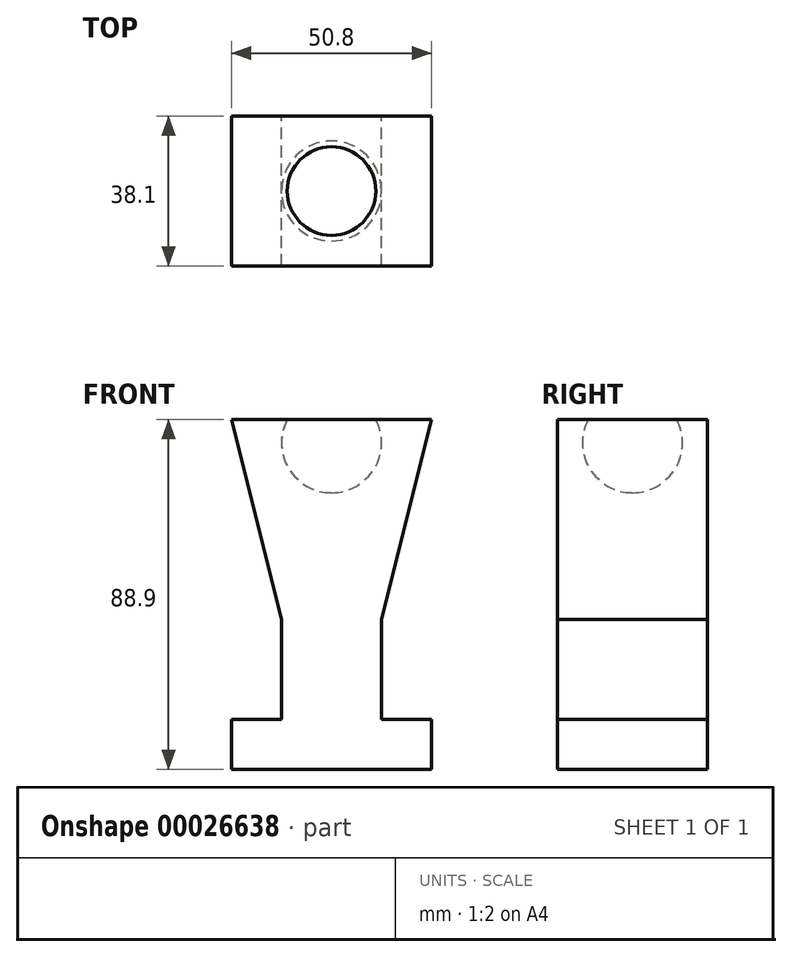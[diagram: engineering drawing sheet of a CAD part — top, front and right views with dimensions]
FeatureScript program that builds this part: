
annotation { "Feature Type Name" : "Feature", "Feature Type Description" : "" }
export const myFeature = defineFeature(function(context is Context, id is Id, definition is map)
    precondition{}
    {
        {
            var Q0;
            Q0=qCreatedBy(makeId("Front.planeOp"),FACE);
            var sketch = newSketch(context, id + "F0", { "sketchPlane" : qUnion([Q0])});
            skLineSegment(sketch, "E0.bottom", {"start": v(-14.34, 69.07) * mm, "end": v(11.06, 69.07) * mm});
            skLineSegment(sketch, "E1", {"start": v(-14.34, 18.27) * mm, "end": v(-14.34, -7.13) * mm});
            skLineSegment(sketch, "E2", {"start": v(-14.34, -7.13) * mm, "end": v(-27.04, -7.13) * mm});
            skLineSegment(sketch, "E3", {"start": v(11.06, -7.13) * mm, "end": v(23.76, -7.13) * mm});
            skLineSegment(sketch, "E4", {"start": v(11.06, 18.27) * mm, "end": v(11.06, -7.13) * mm});
            skLineSegment(sketch, "E5", {"start": v(23.76, -7.13) * mm, "end": v(23.76, -19.83) * mm});
            skLineSegment(sketch, "E6", {"start": v(23.76, -19.83) * mm, "end": v(-27.04, -19.83) * mm});
            skLineSegment(sketch, "E7", {"start": v(-27.04, -19.83) * mm, "end": v(-27.04, -7.13) * mm});
            skPoint(sketch, "E8.orphan", {"position": v(49.16, 69.07) * mm});
            skLineSegment(sketch, "E9", {"start": v(11.06, 69.07) * mm, "end": v(23.76, 69.07) * mm});
            skLineSegment(sketch, "E10", {"start": v(-14.34, 69.07) * mm, "end": v(-27.04, 69.07) * mm});
            skLineSegment(sketch, "E11", {"start": v(11.06, -7.13) * mm, "end": v(11.06, 18.27) * mm});
            skLineSegment(sketch, "E12", {"start": v(11.06, 18.27) * mm, "end": v(23.76, 69.07) * mm});
            skLineSegment(sketch, "E13", {"start": v(-14.34, 18.27) * mm, "end": v(-27.04, 69.07) * mm});
            skLineSegment(sketch, "E14", {"start": v(-27.04, 69.07) * mm, "end": v(23.76, 69.07) * mm});
            skSolve(sketch);
        }
        {
            var Q0;
            Q0=makeQuery(id+"F0.imprint","IMPRINT",FACE,{"disambiguationData":[TD([[makeQuery(id+"F0.imprint","IMPRINT",EDGE,{"derivedFrom":sQuery(id+"F0.wireOp",EDGE,"E1")}),1.0]])]});
            extrude(context, id + "F1", {"entities" : qUnion([Q0]), "depth" : 38.1 * mm});
        }
        {
            var Q0;
            Q0=makeQuery(id+"F1.opExtrude","CAP_FACE",FACE,{"disambiguationData":[OSD([sQuery(id+"F0.wireOp",EDGE,"35849a46-04ca-497c-b77f-f5f883fc5e10"),sQuery(id+"F0.wireOp",EDGE,"E1"),sQuery(id+"F0.wireOp",EDGE,"E2"),sQuery(id+"F0.wireOp",EDGE,"E4"),sQuery(id+"F0.wireOp",EDGE,"E3"),sQuery(id+"F0.wireOp",EDGE,"E5"),sQuery(id+"F0.wireOp",EDGE,"E6"),sQuery(id+"F0.wireOp",EDGE,"E7")])],"isStart":false});
            var Q1;
            Q1=makeQuery(id+"F1.opExtrude","CAP_FACE",FACE,{"disambiguationData":[OSD([sQuery(id+"F0.wireOp",EDGE,"35849a46-04ca-497c-b77f-f5f883fc5e10"),sQuery(id+"F0.wireOp",EDGE,"E1"),sQuery(id+"F0.wireOp",EDGE,"E2"),sQuery(id+"F0.wireOp",EDGE,"E4"),sQuery(id+"F0.wireOp",EDGE,"E3"),sQuery(id+"F0.wireOp",EDGE,"E5"),sQuery(id+"F0.wireOp",EDGE,"E6"),sQuery(id+"F0.wireOp",EDGE,"E7")])],"isStart":true});
            cPlane(context, id + "F2", {"entities" : qUnion([Q0, Q1]), "cplaneType" : CPlaneType.MID_PLANE, "offset" : 152.4 * mm, "width" : 152.4 * mm, "height" : 152.4 * mm});
        }
        {
            var Q0;
            Q0=qCreatedBy(id+"F2.planeOp",FACE);
            var sketch = newSketch(context, id + "F3", { "sketchPlane" : qUnion([Q0])});
            skLineSegment(sketch, "E15", {"start": v(1.94, 67.4) * mm, "end": v(-5.44, 67.4) * mm});
            skLineSegment(sketch, "E16", {"start": v(6.32, 67.5) * mm, "end": v(-9.6, 67.5) * mm});
            skLineSegment(sketch, "E17", {"start": v(6.32, 67.5) * mm, "end": v(-1.64, 67.5) * mm});
            skLineSegment(sketch, "E18", {"start": v(-1.64, 67.5) * mm, "end": v(-1.64, 63.17) * mm});
            skPoint(sketch, "E19.orphan", {"position": v(-19.77, 67.5) * mm});
            skPoint(sketch, "E20.orphan", {"position": v(16.5, 67.5) * mm});
            skArc(sketch, "E21", {"start": v(-1.64, 75.87) * mm, "mid": v(-14.34, 63.17) * mm, "end": v(-1.64, 50.47) * mm});
            skLineSegment(sketch, "E22", {"start": v(-1.64, 63.17) * mm, "end": v(-1.64, 75.87) * mm});
            skLineSegment(sketch, "E23", {"start": v(-1.64, 75.87) * mm, "end": v(-1.64, 50.47) * mm});
            skSolve(sketch);
        }
        {
            var Q0;
            {var subQ1=sQuery(id+"F3.wireOp",EDGE,"E21");Q0=makeQuery(id+"F3.imprint","IMPRINT",FACE,{"disambiguationData":[TD([[makeQuery(id+"F3.imprint","IMPRINT",EDGE,{"derivedFrom":subQ1}),1.0]])]});}
            var Q1;
            Q1=sQuery(id+"F3.wireOp",EDGE,"E23");
            revolve(context, id + "F4", {"operationType" : NewBodyOperationType.REMOVE, "entities" : qUnion([Q0]), "axis" : qUnion([Q1]), "revolveType" : RevolveType.FULL, "oppositeDirection" : true});
        }
    });
